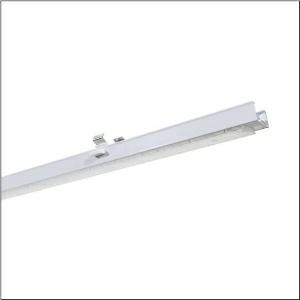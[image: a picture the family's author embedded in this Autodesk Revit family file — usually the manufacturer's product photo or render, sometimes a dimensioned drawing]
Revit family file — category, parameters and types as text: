
# Revit family: trunking_flex_31_51re12mb4cb
name_source: partatom
category: Lighting Fixtures
units: mm (PartAtom-declared; Revit-internal decimal feet)

## family parameters
Cut with Voids When Loaded = No
Host = Face
Light Source = No
Part Type = Normal
Room Calculation Point = No
Round Connector Dimension = Use Diameter
Shared = No

## types (1)
- --- (1 x LED, 11500 lm, 66 W, 4000K)
    Apparent Load = 66 VA
    CIE Flux Codes = 65 91 98 99 100
    Color Rendering = 80
    Color Temperature = 4000K
    Default Elevation = 1800 mm
    Description = Trunking Flex 31, luminaire insert, of extruded aluminium section, coated, traffic white (RAL 9016), length: 1.472mm, width: 91mm, height: 53mm, LED rated luminous flux: 11.500lm, light colour: 840, control gear: ON/OFF Multilumen, with system connector: socket, mains connection: 220..240V, AC, 50/60Hz, rated input power: 66W, connected load according to luminous flux setting (19/24/32/37/47/52/60/66W), luminous flux adjustable on luminaire in eight steps (3450/4380/5800/6700/8350/9200/10500/11500lm ), primary light control with lens, of plastic, primary optical cover: cover, of PMMA, light emission: direct distribution, protection rating (complete): IP20, insulation class (complete): insulation class I (protective earthing), certification: CE, UKCA, impact resistance: IK02, permissible ambient temperature for indoor applications: -20..+40°C, packaging unit: 1 piece
    Height = 58 mm
    Lamp = 1 x LED
    Lamp Light Flux = 11500 lm
    Lamp Power = 66 W
    Lamp count = 1
    Length = 1472 mm
    Luminous efficacy = 174 lm/W
    Manufacturer = Siteco
    ModVariant = No
    Model = 51RE12MB4CB
    Mounting Place = Ceiling
    Mounting Type = Pendant
    Number of Poles = 1
    OnlyDefault = Yes
    Power Factor = 1
    Product Name = Trunking Flex 31
    Product group = luminaire insert
    ProductGroupID = 902
    Protection Class = Protection class I
    Protection Degree = IP 20
    RLX_Detail_Level = 1
    RLX_Emergency_Light_Flux = 0 lm
    RLX_Emergency_Type = 0
    RLX_Emergency_Type_DB = No
    RlxData = <blob elided: 20985 chars, md5=5c9c2b53>
    Socket = socket
    Standby Power = 0 W
    System Light Flux = 11500 lm
    System Power = 66 W
    Type Comments = factory setting: luminous flux: 100 % | (ON | ON | ON)
    Type Image = l_1266702.jpg
    URL = http://relux.com
    VarID = @adj_059150
    Voltage = 0 V
    Weight = 0.00 kg
    Width = 65 mm

## geometry (parser evidence)
native form markers: Blend x4, Sweep x10
no freeform markers — native parametric forms only
